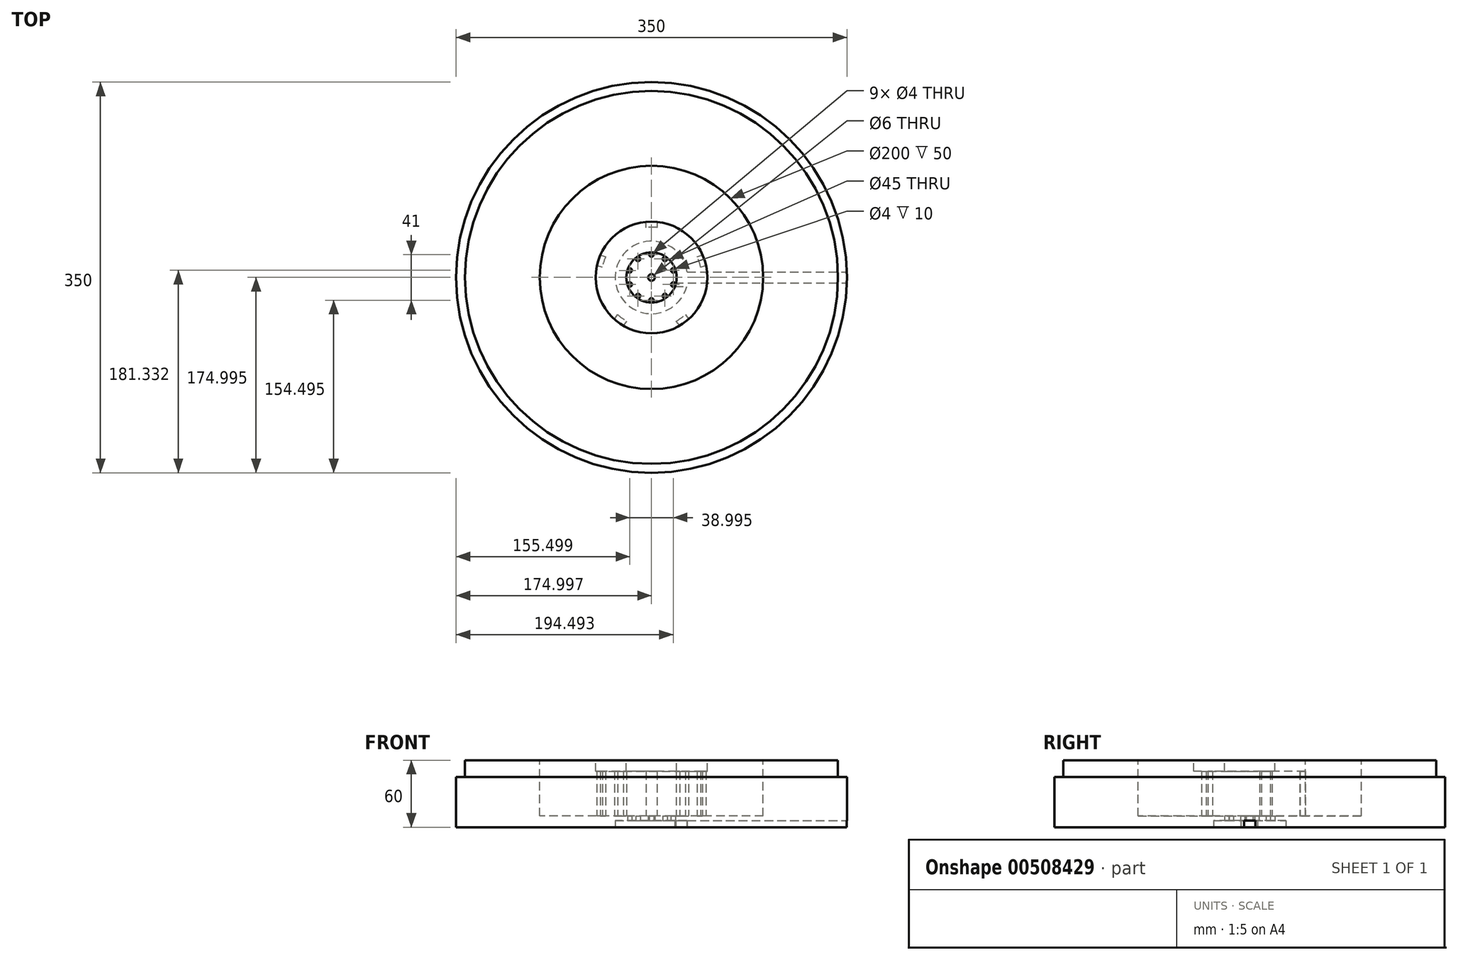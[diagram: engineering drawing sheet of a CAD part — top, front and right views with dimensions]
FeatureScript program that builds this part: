
annotation { "Feature Type Name" : "Feature", "Feature Type Description" : "" }
export const myFeature = defineFeature(function(context is Context, id is Id, definition is map)
    precondition{}
    {
        {
            var Q0;
            Q0=qCreatedBy(makeId("Top.planeOp"),FACE);
            var sketch = newSketch(context, id + "F0", { "sketchPlane" : qUnion([Q0])});
            skCircle(sketch, "E0", {"center": v(-44.55, -28.05) * mm, "radius": 167 * mm});
            skSolve(sketch);
        }
        {
            var Q0;
            Q0 = qSketchRegion(id + "F0", true);
            extrude(context, id + "F1", {"entities" : qUnion([Q0]), "depth" : 50 * mm});
        }
        {
            var Q0;
            Q0=makeQuery(id+"F1.opExtrude","CAP_FACE",FACE,{"disambiguationData":[OSD([sQuery(id+"F0.wireOp",EDGE,"E0")])],"isStart":false});
            var sketch = newSketch(context, id + "F2", { "sketchPlane" : qUnion([Q0])});
            skCircle(sketch, "E1", {"center": v(-44.55, -28.05) * mm, "radius": 168 * mm});
            skCircle(sketch, "E2", {"center": v(-44.55, -28.05) * mm, "radius": 22.5 * mm});
            skCircle(sketch, "E3", {"center": v(-44.55, -28.05) * mm, "radius": 100 * mm});
            skCircle(sketch, "E4", {"center": v(-44.55, -28.05) * mm, "radius": 50 * mm});
            skSolve(sketch);
        }
        {
            var Q0;
            Q0=makeQuery(id+"F2.imprint","IMPRINT",FACE,{"disambiguationData":[TD([[makeQuery(id+"F2.imprint","IMPRINT",EDGE,{"derivedFrom":sQuery(id+"F2.wireOp",EDGE,"E3")}),1.0]])]});
            var Q1;
            Q1=makeQuery(id+"F2.imprint","IMPRINT",FACE,{"disambiguationData":[TD([[makeQuery(id+"F2.imprint","IMPRINT",EDGE,{"derivedFrom":sQuery(id+"F2.wireOp",EDGE,"E2")}),1.0]])]});
            extrude(context, id + "F3", {"entities" : qUnion([Q0, Q1]), "operationType" : NewBodyOperationType.REMOVE, "oppositeDirection" : true, "depth" : 50 * mm});
        }
        {
            var Q0;
            Q0=makeQuery(id+"F3.boolean.opBoolean","SPLIT",FACE,{"disambiguationData":[TD([makeQuery(id+"F3.opExtrude","SWEPT_FACE",FACE,{"disambiguationData":[OSD([sQuery(id+"F2.wireOp",EDGE,"E2")])]})])],"derivedFrom":makeQuery(id+"F1.opExtrude","CAP_FACE",FACE,{"disambiguationData":[OSD([sQuery(id+"F0.wireOp",EDGE,"E0")])],"isStart":false})});
            var sketch = newSketch(context, id + "F4", { "sketchPlane" : qUnion([Q0])});
            skCircle(sketch, "E5", {"center": v(-44.55, -28.05) * mm, "radius": 100 * mm});
            skCircle(sketch, "E6", {"center": v(-44.55, -28.05) * mm, "radius": 50 * mm});
            skCircle(sketch, "E7", {"center": v(-44.55, -28.05) * mm, "radius": 10 * mm});
            skLineSegment(sketch, "E8", {"start": v(-44.55, 21.95) * mm, "end": v(-39.55, 21.95) * mm});
            skLineSegment(sketch, "E9", {"start": v(-39.55, 21.95) * mm, "end": v(-49.55, 21.95) * mm});
            skLineSegment(sketch, "E10", {"start": v(-49.55, 21.95) * mm, "end": v(-49.55, 71.82) * mm});
            skLineSegment(sketch, "E11", {"start": v(-49.55, 71.82) * mm, "end": v(-49.55, -19.4) * mm});
            skLineSegment(sketch, "E12", {"start": v(-49.55, -19.4) * mm, "end": v(-23.79, -19.4) * mm});
            skLineSegment(sketch, "E13", {"start": v(-23.79, -19.4) * mm, "end": v(-39.55, 21.95) * mm});
            skLineSegment(sketch, "E14", {"start": v(-39.55, 71.82) * mm, "end": v(-39.55, 21.95) * mm});
            skLineSegment(sketch, "E15.1.0", {"start": v(52.2, -2.8) * mm, "end": v(4.64, -17.79) * mm});
            skLineSegment(sketch, "E15.1.1", {"start": v(49.2, 6.75) * mm, "end": v(-37.8, -20.68) * mm});
            skLineSegment(sketch, "E15.1.2", {"start": v(-30.05, -45.26) * mm, "end": v(4.64, -17.79) * mm});
            skLineSegment(sketch, "E15.2.0", {"start": v(8.64, -112.74) * mm, "end": v(-19.97, -71.88) * mm});
            skLineSegment(sketch, "E15.2.1", {"start": v(16.83, -107) * mm, "end": v(-35.5, -32.28) * mm});
            skLineSegment(sketch, "E15.2.2", {"start": v(-56.6, -47.06) * mm, "end": v(-19.97, -71.88) * mm});
            skLineSegment(sketch, "E15.3.0", {"start": v(-109.32, -104.25) * mm, "end": v(-78.96, -64.68) * mm});
            skLineSegment(sketch, "E15.3.1", {"start": v(-101.39, -110.33) * mm, "end": v(-45.86, -37.97) * mm});
            skLineSegment(sketch, "E15.3.2", {"start": v(-66.3, -22.28) * mm, "end": v(-78.96, -64.68) * mm});
            skLineSegment(sketch, "E15.4.0", {"start": v(-136.7, 10.8) * mm, "end": v(-89.83, -6.26) * mm});
            skLineSegment(sketch, "E15.4.1", {"start": v(-140.12, 1.4) * mm, "end": v(-54.4, -29.8) * mm});
            skLineSegment(sketch, "E15.4.2", {"start": v(-45.59, -5.58) * mm, "end": v(-89.83, -6.26) * mm});
            skLineSegment(sketch, "E15.anchor1", {"start": v(-44.55, -28.05) * mm, "end": v(-39.55, 21.95) * mm, "construction": true});
            skLineSegment(sketch, "E15.anchor2", {"start": v(-44.55, -28.05) * mm, "end": v(-89.83, -6.26) * mm, "construction": true});
            skSolve(sketch);
        }
        {
            var Q0;
            {var subQ5=sQuery(id+"F4.wireOp",EDGE,"E15.1.0");Q0=makeQuery(id+"F4.imprint","IMPRINT",FACE,{"disambiguationData":[TD([[makeQuery(id+"F4.imprint","IMPRINT",EDGE,{"derivedFrom":subQ5}),-1.0]])]});}
            var Q1;
            {var subQ5=sQuery(id+"F4.wireOp",EDGE,"E15.4.0");Q1=makeQuery(id+"F4.imprint","IMPRINT",FACE,{"disambiguationData":[TD([[makeQuery(id+"F4.imprint","IMPRINT",EDGE,{"derivedFrom":subQ5}),-1.0]])]});}
            var Q2;
            {var subQ0=sQuery(id+"F4.wireOp",EDGE,"E15.3.0");Q2=makeQuery(id+"F4.imprint","IMPRINT",FACE,{"disambiguationData":[TD([[makeQuery(id+"F4.imprint","IMPRINT",EDGE,{"derivedFrom":subQ0}),-1.0]])]});}
            var Q3;
            {var subQ5=sQuery(id+"F4.wireOp",EDGE,"E15.2.0");Q3=makeQuery(id+"F4.imprint","IMPRINT",FACE,{"disambiguationData":[TD([[makeQuery(id+"F4.imprint","IMPRINT",EDGE,{"derivedFrom":subQ5}),-1.0]])]});}
            var Q4;
            {var subQ5=sQuery(id+"F4.wireOp",EDGE,"E14");Q4=makeQuery(id+"F4.imprint","IMPRINT",FACE,{"disambiguationData":[TD([[makeQuery(id+"F4.imprint","IMPRINT",EDGE,{"derivedFrom":subQ5}),-1.0]])]});}
            var Q5;
            {var subQ0=sQuery(id+"F4.wireOp",EDGE,"E13");var subQ1=sQuery(id+"F4.wireOp",EDGE,"E6");var subQ2=makeQuery(id+"F4.imprint","INTERSECT",VERTEX,{"derivedFrom":[subQ1,subQ0]});Q5=makeQuery(id+"F4.imprint","IMPRINT",FACE,{"disambiguationData":[TD([[makeQuery(id+"F4.imprint","IMPRINT",EDGE,{"disambiguationData":[TD([[subQ2,-1.0]])],"derivedFrom":subQ1}),-1.0]])]});}
            var Q6;
            {var subQ0=sQuery(id+"F4.wireOp",EDGE,"E9");var subQ1=sQuery(id+"F4.wireOp",EDGE,"E6");var subQ2=makeQuery(id+"F4.imprint","INTERSECT",VERTEX,{"derivedFrom":[subQ1,subQ0]});Q6=makeQuery(id+"F4.imprint","IMPRINT",FACE,{"disambiguationData":[TD([[makeQuery(id+"F4.imprint","IMPRINT",EDGE,{"disambiguationData":[TD([[subQ2,-1.0]])],"derivedFrom":subQ1}),-1.0]])]});}
            extrude(context, id + "F5", {"entities" : qUnion([Q0, Q1, Q2, Q3, Q4, Q5, Q6]), "operationType" : NewBodyOperationType.ADD, "oppositeDirection" : true, "depth" : 10 * mm, "hasDraft" : true, "draftAngle" : 3 * degree});
        }
        {
            var Q0;
            Q0=makeQuery(id+"F0.imprint","IMPRINT",FACE,{"disambiguationData":[TD([[makeQuery(id+"F0.imprint","IMPRINT",EDGE,{"derivedFrom":sQuery(id+"F0.wireOp",EDGE,"E0")}),1.0]])]});
            var sketch = newSketch(context, id + "F6", { "sketchPlane" : qUnion([Q0])});
            skCircle(sketch, "E16", {"center": v(-44.55, -28.05) * mm, "radius": 50 * mm});
            skCircle(sketch, "E17", {"center": v(-44.55, -28.05) * mm, "radius": 10 * mm});
            skLineSegment(sketch, "E18", {"start": v(-44.55, -28.05) * mm, "end": v(-44.55, 21.95) * mm});
            skLineSegment(sketch, "E19", {"start": v(-44.55, 21.95) * mm, "end": v(-49.55, 21.95) * mm});
            skLineSegment(sketch, "E20", {"start": v(-49.55, 21.95) * mm, "end": v(-39.55, 21.95) * mm});
            skLineSegment(sketch, "E21", {"start": v(-39.55, 21.95) * mm, "end": v(-39.55, -28.05) * mm});
            skLineSegment(sketch, "E22", {"start": v(-39.55, -28.05) * mm, "end": v(-49.55, -28.05) * mm});
            skLineSegment(sketch, "E23", {"start": v(-49.55, -28.05) * mm, "end": v(-49.55, 21.95) * mm});
            skCircle(sketch, "E24", {"center": v(-44.55, -28.05) * mm, "radius": 45 * mm});
            skLineSegment(sketch, "E25.1.0", {"start": v(-46.1, -32.81) * mm, "end": v(-93.65, -17.36) * mm});
            skLineSegment(sketch, "E25.1.1", {"start": v(-93.65, -17.36) * mm, "end": v(-90.56, -7.85) * mm});
            skLineSegment(sketch, "E25.1.3", {"start": v(-90.56, -7.85) * mm, "end": v(-43, -23.3) * mm});
            skLineSegment(sketch, "E25.2.0", {"start": v(-40.5, -31) * mm, "end": v(-69.9, -71.44) * mm});
            skLineSegment(sketch, "E25.2.1", {"start": v(-69.9, -71.44) * mm, "end": v(-77.99, -65.57) * mm});
            skLineSegment(sketch, "E25.2.3", {"start": v(-77.99, -65.57) * mm, "end": v(-48.6, -25.12) * mm});
            skLineSegment(sketch, "E25.3.0", {"start": v(-40.5, -25.12) * mm, "end": v(-11.12, -65.57) * mm});
            skLineSegment(sketch, "E25.3.1", {"start": v(-11.12, -65.57) * mm, "end": v(-19.2, -71.44) * mm});
            skLineSegment(sketch, "E25.3.3", {"start": v(-19.2, -71.44) * mm, "end": v(-48.6, -31) * mm});
            skLineSegment(sketch, "E25.4.0", {"start": v(-46.1, -23.3) * mm, "end": v(1.45, -7.85) * mm});
            skLineSegment(sketch, "E25.4.1", {"start": v(1.45, -7.85) * mm, "end": v(4.54, -17.36) * mm});
            skLineSegment(sketch, "E25.4.3", {"start": v(4.54, -17.36) * mm, "end": v(-43, -32.81) * mm});
            skSolve(sketch);
        }
        {
            var Q0;
            Q0=makeQuery(id+"F6.imprint","IMPRINT",FACE,{"disambiguationData":[TD([[makeQuery(id+"F6.imprint","IMPRINT",EDGE,{"derivedFrom":makeQuery(id+"F0.imprint","IMPRINT",EDGE,{"derivedFrom":sQuery(id+"F0.wireOp",EDGE,"E0")})}),1.0]])]});
            var sketch = newSketch(context, id + "F7", { "sketchPlane" : qUnion([Q0])});
            skSolve(sketch);
        }
        {
            var Q0;
            {var subQ0=sQuery(id+"F6.wireOp",EDGE,"E25.1.0");var subQ1=sQuery(id+"F6.wireOp",EDGE,"E17");var subQ2=makeQuery(id+"F6.imprint","INTERSECT",VERTEX,{"derivedFrom":[subQ1,subQ0]});Q0=makeQuery(id+"F6.imprint","IMPRINT",FACE,{"disambiguationData":[TD([[makeQuery(id+"F6.imprint","IMPRINT",EDGE,{"disambiguationData":[TD([[subQ2,-1.0]])],"derivedFrom":subQ1}),-1.0]])]});}
            var Q1;
            {var subQ0=sQuery(id+"F6.wireOp",EDGE,"E21");var subQ1=sQuery(id+"F6.wireOp",EDGE,"E17");var subQ2=makeQuery(id+"F6.imprint","INTERSECT",VERTEX,{"derivedFrom":[subQ1,subQ0]});Q1=makeQuery(id+"F6.imprint","IMPRINT",FACE,{"disambiguationData":[TD([[makeQuery(id+"F6.imprint","IMPRINT",EDGE,{"disambiguationData":[TD([[subQ2,1.0]])],"derivedFrom":subQ1}),-1.0]])]});}
            var Q2;
            {var subQ0=sQuery(id+"F6.wireOp",EDGE,"E21");var subQ1=sQuery(id+"F6.wireOp",EDGE,"E17");var subQ2=makeQuery(id+"F6.imprint","INTERSECT",VERTEX,{"derivedFrom":[subQ1,subQ0]});Q2=makeQuery(id+"F6.imprint","IMPRINT",FACE,{"disambiguationData":[TD([[makeQuery(id+"F6.imprint","IMPRINT",EDGE,{"disambiguationData":[TD([[subQ2,-1.0]])],"derivedFrom":subQ1}),-1.0]])]});}
            var Q3;
            {var subQ0=sQuery(id+"F6.wireOp",EDGE,"E18");var subQ1=sQuery(id+"F6.wireOp",EDGE,"E17");var subQ2=makeQuery(id+"F6.imprint","INTERSECT",VERTEX,{"derivedFrom":[subQ1,subQ0]});Q3=makeQuery(id+"F6.imprint","IMPRINT",FACE,{"disambiguationData":[TD([[makeQuery(id+"F6.imprint","IMPRINT",EDGE,{"disambiguationData":[TD([[subQ2,-1.0]])],"derivedFrom":subQ1}),-1.0]])]});}
            var Q4;
            {var subQ0=sQuery(id+"F6.wireOp",EDGE,"E23");var subQ1=sQuery(id+"F6.wireOp",EDGE,"E17");var subQ2=makeQuery(id+"F6.imprint","INTERSECT",VERTEX,{"derivedFrom":[subQ1,subQ0]});Q4=makeQuery(id+"F6.imprint","IMPRINT",FACE,{"disambiguationData":[TD([[makeQuery(id+"F6.imprint","IMPRINT",EDGE,{"disambiguationData":[TD([[subQ2,-1.0]])],"derivedFrom":subQ1}),-1.0]])]});}
            var Q5;
            {var subQ0=sQuery(id+"F6.wireOp",EDGE,"E25.1.3");var subQ1=sQuery(id+"F6.wireOp",EDGE,"E17");var subQ2=makeQuery(id+"F6.imprint","INTERSECT",VERTEX,{"derivedFrom":[subQ1,subQ0]});Q5=makeQuery(id+"F6.imprint","IMPRINT",FACE,{"disambiguationData":[TD([[makeQuery(id+"F6.imprint","IMPRINT",EDGE,{"disambiguationData":[TD([[subQ2,-1.0]])],"derivedFrom":subQ1}),-1.0]])]});}
            var Q6;
            {var subQ0=sQuery(id+"F6.wireOp",EDGE,"E25.2.3");var subQ1=sQuery(id+"F6.wireOp",EDGE,"E17");var subQ2=makeQuery(id+"F6.imprint","INTERSECT",VERTEX,{"derivedFrom":[subQ1,subQ0]});Q6=makeQuery(id+"F6.imprint","IMPRINT",FACE,{"disambiguationData":[TD([[makeQuery(id+"F6.imprint","IMPRINT",EDGE,{"disambiguationData":[TD([[subQ2,-1.0]])],"derivedFrom":subQ1}),-1.0]])]});}
            var Q7;
            {var subQ0=sQuery(id+"F6.wireOp",EDGE,"E25.2.0");var subQ1=sQuery(id+"F6.wireOp",EDGE,"E16");var subQ2=makeQuery(id+"F6.imprint","INTERSECT",VERTEX,{"derivedFrom":[subQ1,subQ0]});Q7=makeQuery(id+"F6.imprint","IMPRINT",FACE,{"disambiguationData":[TD([[makeQuery(id+"F6.imprint","IMPRINT",EDGE,{"disambiguationData":[TD([[subQ2,-1.0]])],"derivedFrom":subQ1}),1.0]])]});}
            var Q8;
            {var subQ0=sQuery(id+"F6.wireOp",EDGE,"E25.2.0");var subQ1=sQuery(id+"F6.wireOp",EDGE,"E17");var subQ2=makeQuery(id+"F6.imprint","INTERSECT",VERTEX,{"derivedFrom":[subQ1,subQ0]});Q8=makeQuery(id+"F6.imprint","IMPRINT",FACE,{"disambiguationData":[TD([[makeQuery(id+"F6.imprint","IMPRINT",EDGE,{"disambiguationData":[TD([[subQ2,-1.0]])],"derivedFrom":subQ1}),-1.0]])]});}
            var Q9;
            {var subQ0=sQuery(id+"F6.wireOp",EDGE,"E25.3.3");var subQ1=sQuery(id+"F6.wireOp",EDGE,"E17");var subQ2=makeQuery(id+"F6.imprint","INTERSECT",VERTEX,{"derivedFrom":[subQ1,subQ0]});Q9=makeQuery(id+"F6.imprint","IMPRINT",FACE,{"disambiguationData":[TD([[makeQuery(id+"F6.imprint","IMPRINT",EDGE,{"disambiguationData":[TD([[subQ2,-1.0]])],"derivedFrom":subQ1}),-1.0]])]});}
            var Q10;
            {var subQ0=sQuery(id+"F6.wireOp",EDGE,"E25.3.0");var subQ1=sQuery(id+"F6.wireOp",EDGE,"E17");var subQ2=makeQuery(id+"F6.imprint","INTERSECT",VERTEX,{"derivedFrom":[subQ1,subQ0]});Q10=makeQuery(id+"F6.imprint","IMPRINT",FACE,{"disambiguationData":[TD([[makeQuery(id+"F6.imprint","IMPRINT",EDGE,{"disambiguationData":[TD([[subQ2,-1.0]])],"derivedFrom":subQ1}),-1.0]])]});}
            var Q11;
            {var subQ0=sQuery(id+"F6.wireOp",EDGE,"E25.4.0");var subQ1=sQuery(id+"F6.wireOp",EDGE,"E17");var subQ2=makeQuery(id+"F6.imprint","INTERSECT",VERTEX,{"derivedFrom":[subQ1,subQ0]});Q11=makeQuery(id+"F6.imprint","IMPRINT",FACE,{"disambiguationData":[TD([[makeQuery(id+"F6.imprint","IMPRINT",EDGE,{"disambiguationData":[TD([[subQ2,1.0]])],"derivedFrom":subQ1}),-1.0]])]});}
            var Q12;
            {var subQ0=sQuery(id+"F6.wireOp",EDGE,"E25.4.3");var subQ1=sQuery(id+"F6.wireOp",EDGE,"E16");var subQ2=makeQuery(id+"F6.imprint","INTERSECT",VERTEX,{"derivedFrom":[subQ1,subQ0]});Q12=makeQuery(id+"F6.imprint","IMPRINT",FACE,{"disambiguationData":[TD([[makeQuery(id+"F6.imprint","IMPRINT",EDGE,{"disambiguationData":[TD([[subQ2,1.0]])],"derivedFrom":subQ1}),1.0]])]});}
            var Q13;
            {var subQ0=sQuery(id+"F6.wireOp",EDGE,"E25.4.0");var subQ1=sQuery(id+"F6.wireOp",EDGE,"E16");var subQ2=makeQuery(id+"F6.imprint","INTERSECT",VERTEX,{"derivedFrom":[subQ1,subQ0]});Q13=makeQuery(id+"F6.imprint","IMPRINT",FACE,{"disambiguationData":[TD([[makeQuery(id+"F6.imprint","IMPRINT",EDGE,{"disambiguationData":[TD([[subQ2,-1.0]])],"derivedFrom":subQ1}),1.0]])]});}
            var Q14;
            {var subQ0=sQuery(id+"F6.wireOp",EDGE,"E23");var subQ1=sQuery(id+"F6.wireOp",EDGE,"E16");var subQ2=makeQuery(id+"F6.imprint","INTERSECT",VERTEX,{"derivedFrom":[subQ1,subQ0]});Q14=makeQuery(id+"F6.imprint","IMPRINT",FACE,{"disambiguationData":[TD([[makeQuery(id+"F6.imprint","IMPRINT",EDGE,{"disambiguationData":[TD([[subQ2,-1.0]])],"derivedFrom":subQ1}),1.0]])]});}
            var Q15;
            {var subQ0=sQuery(id+"F6.wireOp",EDGE,"E25.1.0");var subQ1=sQuery(id+"F6.wireOp",EDGE,"E16");var subQ2=makeQuery(id+"F6.imprint","INTERSECT",VERTEX,{"derivedFrom":[subQ1,subQ0]});Q15=makeQuery(id+"F6.imprint","IMPRINT",FACE,{"disambiguationData":[TD([[makeQuery(id+"F6.imprint","IMPRINT",EDGE,{"disambiguationData":[TD([[subQ2,-1.0]])],"derivedFrom":subQ1}),1.0]])]});}
            extrude(context, id + "F8", {"entities" : qUnion([Q0, Q1, Q2, Q3, Q4, Q5, Q6, Q7, Q8, Q9, Q10, Q11, Q12, Q13, Q14, Q15]), "operationType" : NewBodyOperationType.REMOVE, "depth" : 40 * mm});
        }
        {
            var Q0;
            Q0=makeQuery(id+"F7.imprint","IMPRINT",FACE,{"disambiguationData":[TD([[makeQuery(id+"F7.imprint","IMPRINT",EDGE,{"derivedFrom":makeQuery(id+"F6.imprint","IMPRINT",EDGE,{"derivedFrom":makeQuery(id+"F0.imprint","IMPRINT",EDGE,{"derivedFrom":sQuery(id+"F0.wireOp",EDGE,"E0")})})}),1.0]])]});
            var sketch = newSketch(context, id + "F9", { "sketchPlane" : qUnion([Q0])});
            skCircle(sketch, "E26", {"center": v(-44.55, -28.05) * mm, "radius": 100 * mm});
            skCircle(sketch, "E27", {"center": v(-44.55, -28.05) * mm, "radius": 167 * mm});
            skCircle(sketch, "E28", {"center": v(-44.55, -28.05) * mm, "radius": 10 * mm});
            skCircle(sketch, "E29", {"center": v(-44.55, -28.05) * mm, "radius": 50 * mm});
            skSolve(sketch);
        }
        {
            var Q0;
            Q0 = qSketchRegion(id + "F9", true);
            var Q1;
            Q1=makeQuery(id+"F9.imprint","IMPRINT",FACE,{"disambiguationData":[TD([[makeQuery(id+"F9.imprint","IMPRINT",EDGE,{"derivedFrom":sQuery(id+"F9.wireOp",EDGE,"E26")}),1.0]])]});
            var Q2;
            {var subQ1=sQuery(id+"F6.wireOp",EDGE,"E25.4.0");var subQ3=sQuery(id+"F6.wireOp",EDGE,"E16");var subQ4=makeQuery(id+"F6.imprint","INTERSECT",VERTEX,{"derivedFrom":[subQ3,subQ1]});Q2=makeQuery(id+"F7.imprint","IMPRINT",FACE,{"disambiguationData":[TD([[makeQuery(id+"F7.imprint","IMPRINT",EDGE,{"derivedFrom":makeQuery(id+"F6.imprint","IMPRINT",EDGE,{"disambiguationData":[TD([[subQ4,-1.0]])],"derivedFrom":subQ3})}),1.0]])]});}
            extrude(context, id + "F10", {"entities" : qUnion([Q0, Q1, Q2]), "operationType" : NewBodyOperationType.ADD, "oppositeDirection" : true, "depth" : 10 * mm});
        }
        {
            var Q0;
            {var subQ0=sQuery(id+"F4.wireOp",EDGE,"E6");var subQ1=sQuery(id+"F4.wireOp",EDGE,"E5");var subQ2=sQuery(id+"F0.wireOp",EDGE,"E0");var subQ3=makeQuery(id+"F1.opExtrude","CAP_FACE",FACE,{"disambiguationData":[OSD([subQ2])],"isStart":false});Q0=makeQuery(id+"F5.boolean.opBoolean","MERGE",FACE,{"derivedFrom":[makeQuery(id+"F3.boolean.opBoolean","SPLIT",FACE,{"disambiguationData":[TD([makeQuery(id+"F1.opExtrude","SWEPT_FACE",FACE,{"disambiguationData":[OSD([subQ2])]})])],"derivedFrom":subQ3}),makeQuery(id+"F3.boolean.opBoolean","SPLIT",FACE,{"disambiguationData":[TD([makeQuery(id+"F3.opExtrude","SWEPT_FACE",FACE,{"disambiguationData":[OSD([sQuery(id+"F2.wireOp",EDGE,"E2")])]})])],"derivedFrom":subQ3}),makeQuery(id+"F5.opExtrude","CAP_FACE",FACE,{"disambiguationData":[OSD([subQ1,subQ0,sQuery(id+"F4.wireOp",EDGE,"E15.1.0"),sQuery(id+"F4.wireOp",EDGE,"E15.1.1"),sQuery(id+"F4.wireOp",EDGE,"E15.1.2")])],"isStart":true}),makeQuery(id+"F5.opExtrude","CAP_FACE",FACE,{"disambiguationData":[OSD([subQ1,subQ0,sQuery(id+"F4.wireOp",EDGE,"E11"),sQuery(id+"F4.wireOp",EDGE,"E13"),sQuery(id+"F4.wireOp",EDGE,"E14")])],"isStart":true}),makeQuery(id+"F5.opExtrude","CAP_FACE",FACE,{"disambiguationData":[OSD([subQ1,subQ0,sQuery(id+"F4.wireOp",EDGE,"E15.4.0"),sQuery(id+"F4.wireOp",EDGE,"E15.4.1"),sQuery(id+"F4.wireOp",EDGE,"E15.4.2")])],"isStart":true}),makeQuery(id+"F5.opExtrude","CAP_FACE",FACE,{"disambiguationData":[OSD([subQ1,subQ0,sQuery(id+"F4.wireOp",EDGE,"E15.3.0"),sQuery(id+"F4.wireOp",EDGE,"E15.3.1"),sQuery(id+"F4.wireOp",EDGE,"E15.3.2")])],"isStart":true}),makeQuery(id+"F5.opExtrude","CAP_FACE",FACE,{"disambiguationData":[OSD([subQ1,subQ0,sQuery(id+"F4.wireOp",EDGE,"E15.2.0"),sQuery(id+"F4.wireOp",EDGE,"E15.2.1"),sQuery(id+"F4.wireOp",EDGE,"E15.2.2")])],"isStart":true})]});}
            var sketch = newSketch(context, id + "F11", { "sketchPlane" : qUnion([Q0])});
            skCircle(sketch, "E30", {"center": v(-44.55, -28.05) * mm, "radius": 100 * mm});
            skCircle(sketch, "E31", {"center": v(-44.55, -28.05) * mm, "radius": 50 * mm});
            skSolve(sketch);
        }
        {
            var Q0;
            Q0 = qSketchRegion(id + "F11", true);
            extrude(context, id + "F12", {"entities" : qUnion([Q0]), "operationType" : NewBodyOperationType.REMOVE, "oppositeDirection" : true, "depth" : 33 * mm});
        }
        {
            var Q0;
            {var subQ0=sQuery(id+"F6.wireOp",EDGE,"E25.4.3");var subQ1=sQuery(id+"F6.wireOp",EDGE,"E25.4.1");var subQ2=sQuery(id+"F6.wireOp",EDGE,"E25.4.0");var subQ3=sQuery(id+"F6.wireOp",EDGE,"E25.3.3");var subQ4=sQuery(id+"F6.wireOp",EDGE,"E25.3.1");var subQ5=sQuery(id+"F6.wireOp",EDGE,"E25.3.0");var subQ6=sQuery(id+"F6.wireOp",EDGE,"E25.2.3");var subQ7=sQuery(id+"F6.wireOp",EDGE,"E25.2.1");var subQ8=sQuery(id+"F6.wireOp",EDGE,"E25.2.0");var subQ9=sQuery(id+"F6.wireOp",EDGE,"E25.1.3");var subQ10=sQuery(id+"F6.wireOp",EDGE,"E25.1.1");var subQ11=sQuery(id+"F6.wireOp",EDGE,"E25.1.0");var subQ12=sQuery(id+"F6.wireOp",EDGE,"E23");var subQ13=sQuery(id+"F6.wireOp",EDGE,"E21");var subQ14=sQuery(id+"F6.wireOp",EDGE,"E20");Q0=makeQuery(id+"F10.boolean.opBoolean","MERGE",FACE,{"derivedFrom":[makeQuery(id+"F10.opExtrude","CAP_FACE",FACE,{"disambiguationData":[OSD([sQuery(id+"F6.wireOp",EDGE,"E16"),subQ14,subQ13,subQ12,subQ11,subQ10,subQ9,subQ8,subQ7,subQ6,subQ5,subQ4,subQ3,subQ2,subQ1,subQ0])],"isStart":false}),makeQuery(id+"F10.opExtrude","CAP_FACE",FACE,{"disambiguationData":[OSD([subQ14,subQ13,subQ12,subQ11,subQ10,subQ9,subQ8,subQ7,subQ6,subQ5,subQ4,subQ3,subQ2,subQ1,subQ0,sQuery(id+"F9.wireOp",EDGE,"E27"),sQuery(id+"F9.wireOp",EDGE,"E29")])],"isStart":false})]});}
            var sketch = newSketch(context, id + "F13", { "sketchPlane" : qUnion([Q0])});
            skCircle(sketch, "E32", {"center": v(-44.55, 28.05) * mm, "radius": 167 * mm});
            skCircle(sketch, "E33", {"center": v(-44.55, 28.05) * mm, "radius": 175 * mm});
            skSolve(sketch);
        }
        {
            var Q0;
            Q0 = qSketchRegion(id + "F13", true);
            extrude(context, id + "F14", {"entities" : qUnion([Q0]), "operationType" : NewBodyOperationType.ADD, "oppositeDirection" : true, "depth" : 45 * mm});
        }
        {
            var Q0;
            {var subQ0=sQuery(id+"F6.wireOp",EDGE,"E25.4.3");var subQ1=sQuery(id+"F6.wireOp",EDGE,"E25.4.1");var subQ2=sQuery(id+"F6.wireOp",EDGE,"E25.4.0");var subQ3=sQuery(id+"F6.wireOp",EDGE,"E25.3.3");var subQ4=sQuery(id+"F6.wireOp",EDGE,"E25.3.1");var subQ5=sQuery(id+"F6.wireOp",EDGE,"E25.3.0");var subQ6=sQuery(id+"F6.wireOp",EDGE,"E25.2.3");var subQ7=sQuery(id+"F6.wireOp",EDGE,"E25.2.1");var subQ8=sQuery(id+"F6.wireOp",EDGE,"E25.2.0");var subQ9=sQuery(id+"F6.wireOp",EDGE,"E25.1.3");var subQ10=sQuery(id+"F6.wireOp",EDGE,"E25.1.1");var subQ11=sQuery(id+"F6.wireOp",EDGE,"E25.1.0");var subQ12=sQuery(id+"F6.wireOp",EDGE,"E23");var subQ13=sQuery(id+"F6.wireOp",EDGE,"E21");var subQ14=sQuery(id+"F6.wireOp",EDGE,"E20");Q0=makeQuery(id+"F14.boolean.opBoolean","MERGE",FACE,{"derivedFrom":[makeQuery(id+"F10.boolean.opBoolean","MERGE",FACE,{"derivedFrom":[makeQuery(id+"F10.opExtrude","CAP_FACE",FACE,{"disambiguationData":[OSD([sQuery(id+"F6.wireOp",EDGE,"E16"),subQ14,subQ13,subQ12,subQ11,subQ10,subQ9,subQ8,subQ7,subQ6,subQ5,subQ4,subQ3,subQ2,subQ1,subQ0])],"isStart":false}),makeQuery(id+"F10.opExtrude","CAP_FACE",FACE,{"disambiguationData":[OSD([subQ14,subQ13,subQ12,subQ11,subQ10,subQ9,subQ8,subQ7,subQ6,subQ5,subQ4,subQ3,subQ2,subQ1,subQ0,sQuery(id+"F9.wireOp",EDGE,"E27"),sQuery(id+"F9.wireOp",EDGE,"E29")])],"isStart":false})]}),makeQuery(id+"F14.opExtrude","CAP_FACE",FACE,{"disambiguationData":[OSD([sQuery(id+"F13.wireOp",EDGE,"E32"),sQuery(id+"F13.wireOp",EDGE,"E33")])],"isStart":true})]});}
            var sketch = newSketch(context, id + "F15", { "sketchPlane" : qUnion([Q0])});
            skCircle(sketch, "E34", {"center": v(-44.55, 28.05) * mm, "radius": 175 * mm});
            skCircle(sketch, "E35", {"center": v(-44.55, 28.05) * mm, "radius": 3 * mm});
            skSolve(sketch);
        }
        {
            var Q0;
            Q0=makeQuery(id+"F15.imprint","IMPRINT",FACE,{"disambiguationData":[TD([[makeQuery(id+"F15.imprint","IMPRINT",EDGE,{"derivedFrom":sQuery(id+"F15.wireOp",EDGE,"E35")}),1.0]])]});
            extrude(context, id + "F16", {"entities" : qUnion([Q0]), "operationType" : NewBodyOperationType.REMOVE, "oppositeDirection" : true, "depth" : 151 * mm});
        }
        {
            var Q0;
            {var subQ0=sQuery(id+"F6.wireOp",EDGE,"E25.4.3");var subQ1=sQuery(id+"F6.wireOp",EDGE,"E25.4.1");var subQ2=sQuery(id+"F6.wireOp",EDGE,"E25.4.0");var subQ3=sQuery(id+"F6.wireOp",EDGE,"E25.3.3");var subQ4=sQuery(id+"F6.wireOp",EDGE,"E25.3.1");var subQ5=sQuery(id+"F6.wireOp",EDGE,"E25.3.0");var subQ6=sQuery(id+"F6.wireOp",EDGE,"E25.2.3");var subQ7=sQuery(id+"F6.wireOp",EDGE,"E25.2.1");var subQ8=sQuery(id+"F6.wireOp",EDGE,"E25.2.0");var subQ9=sQuery(id+"F6.wireOp",EDGE,"E25.1.3");var subQ10=sQuery(id+"F6.wireOp",EDGE,"E25.1.1");var subQ11=sQuery(id+"F6.wireOp",EDGE,"E25.1.0");var subQ12=sQuery(id+"F6.wireOp",EDGE,"E23");var subQ13=sQuery(id+"F6.wireOp",EDGE,"E21");var subQ14=sQuery(id+"F6.wireOp",EDGE,"E20");Q0=makeQuery(id+"F14.boolean.opBoolean","MERGE",FACE,{"derivedFrom":[makeQuery(id+"F10.boolean.opBoolean","MERGE",FACE,{"derivedFrom":[makeQuery(id+"F10.opExtrude","CAP_FACE",FACE,{"disambiguationData":[OSD([sQuery(id+"F6.wireOp",EDGE,"E16"),subQ14,subQ13,subQ12,subQ11,subQ10,subQ9,subQ8,subQ7,subQ6,subQ5,subQ4,subQ3,subQ2,subQ1,subQ0])],"isStart":false}),makeQuery(id+"F10.opExtrude","CAP_FACE",FACE,{"disambiguationData":[OSD([subQ14,subQ13,subQ12,subQ11,subQ10,subQ9,subQ8,subQ7,subQ6,subQ5,subQ4,subQ3,subQ2,subQ1,subQ0,sQuery(id+"F9.wireOp",EDGE,"E27"),sQuery(id+"F9.wireOp",EDGE,"E29")])],"isStart":false})]}),makeQuery(id+"F14.opExtrude","CAP_FACE",FACE,{"disambiguationData":[OSD([sQuery(id+"F13.wireOp",EDGE,"E32"),sQuery(id+"F13.wireOp",EDGE,"E33")])],"isStart":true})]});}
            var sketch = newSketch(context, id + "F17", { "sketchPlane" : qUnion([Q0])});
            skLineSegment(sketch, "E36.bottom", {"start": v(-44.55, 28.05) * mm, "end": v(153.3, 28.05) * mm});
            skLineSegment(sketch, "E36.top", {"start": v(-44.55, 33.05) * mm, "end": v(153.3, 33.05) * mm});
            skLineSegment(sketch, "E36.left", {"start": v(-44.55, 28.05) * mm, "end": v(-44.55, 33.05) * mm});
            skLineSegment(sketch, "E36.right", {"start": v(153.3, 28.05) * mm, "end": v(153.3, 33.05) * mm});
            skLineSegment(sketch, "E37.bottom", {"start": v(-44.55, 28.05) * mm, "end": v(156.7, 28.05) * mm});
            skLineSegment(sketch, "E37.top", {"start": v(-44.55, 23.05) * mm, "end": v(156.7, 23.05) * mm});
            skLineSegment(sketch, "E37.left", {"start": v(-44.55, 28.05) * mm, "end": v(-44.55, 23.05) * mm});
            skLineSegment(sketch, "E37.right", {"start": v(156.7, 28.05) * mm, "end": v(156.7, 23.05) * mm});
            skSolve(sketch);
        }
        {
            var Q0;
            Q0 = qSketchRegion(id + "F17", true);
            extrude(context, id + "F18", {"entities" : qUnion([Q0]), "operationType" : NewBodyOperationType.REMOVE, "oppositeDirection" : true, "depth" : 6 * mm});
        }
        {
            var Q0;
            {var subQ0=sQuery(id+"F6.wireOp",EDGE,"E25.4.3");var subQ1=sQuery(id+"F6.wireOp",EDGE,"E25.4.1");var subQ2=sQuery(id+"F6.wireOp",EDGE,"E25.4.0");var subQ3=sQuery(id+"F6.wireOp",EDGE,"E25.3.3");var subQ4=sQuery(id+"F6.wireOp",EDGE,"E25.3.1");var subQ5=sQuery(id+"F6.wireOp",EDGE,"E25.3.0");var subQ6=sQuery(id+"F6.wireOp",EDGE,"E25.2.3");var subQ7=sQuery(id+"F6.wireOp",EDGE,"E25.2.1");var subQ8=sQuery(id+"F6.wireOp",EDGE,"E25.2.0");var subQ9=sQuery(id+"F6.wireOp",EDGE,"E25.1.3");var subQ10=sQuery(id+"F6.wireOp",EDGE,"E25.1.1");var subQ11=sQuery(id+"F6.wireOp",EDGE,"E25.1.0");var subQ12=sQuery(id+"F6.wireOp",EDGE,"E23");var subQ13=sQuery(id+"F6.wireOp",EDGE,"E21");var subQ14=sQuery(id+"F6.wireOp",EDGE,"E20");Q0=makeQuery(id+"F14.boolean.opBoolean","MERGE",FACE,{"derivedFrom":[makeQuery(id+"F10.boolean.opBoolean","MERGE",FACE,{"derivedFrom":[makeQuery(id+"F10.opExtrude","CAP_FACE",FACE,{"disambiguationData":[OSD([sQuery(id+"F6.wireOp",EDGE,"E16"),subQ14,subQ13,subQ12,subQ11,subQ10,subQ9,subQ8,subQ7,subQ6,subQ5,subQ4,subQ3,subQ2,subQ1,subQ0])],"isStart":false}),makeQuery(id+"F10.opExtrude","CAP_FACE",FACE,{"disambiguationData":[OSD([subQ14,subQ13,subQ12,subQ11,subQ10,subQ9,subQ8,subQ7,subQ6,subQ5,subQ4,subQ3,subQ2,subQ1,subQ0,sQuery(id+"F9.wireOp",EDGE,"E27"),sQuery(id+"F9.wireOp",EDGE,"E29")])],"isStart":false})]}),makeQuery(id+"F14.opExtrude","CAP_FACE",FACE,{"disambiguationData":[OSD([sQuery(id+"F13.wireOp",EDGE,"E32"),sQuery(id+"F13.wireOp",EDGE,"E33")])],"isStart":true})]});}
            var sketch = newSketch(context, id + "F19", { "sketchPlane" : qUnion([Q0])});
            skCircle(sketch, "E38", {"center": v(-25.06, 34.39) * mm, "radius": 2 * mm});
            skCircle(sketch, "E39.1.0", {"center": v(-32.5, 44.64) * mm, "radius": 2 * mm});
            skCircle(sketch, "E39.2.0", {"center": v(-44.55, 48.55) * mm, "radius": 2 * mm});
            skCircle(sketch, "E39.3.0", {"center": v(-56.6, 44.64) * mm, "radius": 2 * mm});
            skCircle(sketch, "E39.4.0", {"center": v(-64.05, 34.4) * mm, "radius": 2 * mm});
            skCircle(sketch, "E39.5.0", {"center": v(-64.05, 21.72) * mm, "radius": 2 * mm});
            skCircle(sketch, "E39.6.0", {"center": v(-56.6, 11.47) * mm, "radius": 2 * mm});
            skCircle(sketch, "E39.7.0", {"center": v(-44.56, 7.55) * mm, "radius": 2 * mm});
            skCircle(sketch, "E39.8.0", {"center": v(-32.5, 11.47) * mm, "radius": 2 * mm});
            skCircle(sketch, "E39.9.0", {"center": v(-25.06, 21.72) * mm, "radius": 2 * mm});
            skPoint(sketch, "E39.center", {"position": v(-44.55, 28.05) * mm});
            skLineSegment(sketch, "E40", {"start": v(-24.53, 32.46) * mm, "end": v(-24.38, 33.05) * mm});
            skLineSegment(sketch, "E41", {"start": v(-24.38, 33.05) * mm, "end": v(-24.27, 23.05) * mm});
            skLineSegment(sketch, "E42", {"start": v(-24.27, 23.05) * mm, "end": v(-24.48, 23.63) * mm});
            skSolve(sketch);
        }
        {
            var Q0;
            Q0 = qSketchRegion(id + "F19", true);
            extrude(context, id + "F20", {"entities" : qUnion([Q0]), "operationType" : NewBodyOperationType.REMOVE, "oppositeDirection" : true, "depth" : 219 * mm});
        }
        {
            var Q0;
            {var subQ0=sQuery(id+"F6.wireOp",EDGE,"E25.4.3");var subQ1=sQuery(id+"F6.wireOp",EDGE,"E25.4.1");var subQ2=sQuery(id+"F6.wireOp",EDGE,"E25.4.0");var subQ3=sQuery(id+"F6.wireOp",EDGE,"E25.3.3");var subQ4=sQuery(id+"F6.wireOp",EDGE,"E25.3.1");var subQ5=sQuery(id+"F6.wireOp",EDGE,"E25.3.0");var subQ6=sQuery(id+"F6.wireOp",EDGE,"E25.2.3");var subQ7=sQuery(id+"F6.wireOp",EDGE,"E25.2.1");var subQ8=sQuery(id+"F6.wireOp",EDGE,"E25.2.0");var subQ9=sQuery(id+"F6.wireOp",EDGE,"E25.1.3");var subQ10=sQuery(id+"F6.wireOp",EDGE,"E25.1.1");var subQ11=sQuery(id+"F6.wireOp",EDGE,"E25.1.0");var subQ12=sQuery(id+"F6.wireOp",EDGE,"E23");var subQ13=sQuery(id+"F6.wireOp",EDGE,"E21");var subQ14=sQuery(id+"F6.wireOp",EDGE,"E20");Q0=makeQuery(id+"F14.boolean.opBoolean","MERGE",FACE,{"derivedFrom":[makeQuery(id+"F10.boolean.opBoolean","MERGE",FACE,{"derivedFrom":[makeQuery(id+"F10.opExtrude","CAP_FACE",FACE,{"disambiguationData":[OSD([sQuery(id+"F6.wireOp",EDGE,"E16"),subQ14,subQ13,subQ12,subQ11,subQ10,subQ9,subQ8,subQ7,subQ6,subQ5,subQ4,subQ3,subQ2,subQ1,subQ0])],"isStart":false}),makeQuery(id+"F10.opExtrude","CAP_FACE",FACE,{"disambiguationData":[OSD([subQ14,subQ13,subQ12,subQ11,subQ10,subQ9,subQ8,subQ7,subQ6,subQ5,subQ4,subQ3,subQ2,subQ1,subQ0,sQuery(id+"F9.wireOp",EDGE,"E27"),sQuery(id+"F9.wireOp",EDGE,"E29")])],"isStart":false})]}),makeQuery(id+"F14.opExtrude","CAP_FACE",FACE,{"disambiguationData":[OSD([sQuery(id+"F13.wireOp",EDGE,"E32"),sQuery(id+"F13.wireOp",EDGE,"E33")])],"isStart":true})]});}
            var sketch = newSketch(context, id + "F21", { "sketchPlane" : qUnion([Q0])});
            skCircle(sketch, "E43", {"center": v(-44.55, 28.05) * mm, "radius": 22.5 * mm});
            skCircle(sketch, "E44.0", {"center": v(-44.55, 28.05) * mm, "radius": 32.5 * mm});
            skArc(sketch, "E45.0", {"start": v(-44.55, 20.05) * mm, "mid": v(-52.55, 28.05) * mm, "end": v(-44.55, 36.05) * mm});
            skLineSegment(sketch, "E45.1", {"start": v(125.26, 20.05) * mm, "end": v(-44.55, 20.05) * mm});
            skArc(sketch, "E45.2", {"start": v(125.26, 36.05) * mm, "mid": v(-214.55, 28.05) * mm, "end": v(125.26, 20.05) * mm});
            skLineSegment(sketch, "E45.3", {"start": v(-44.55, 36.05) * mm, "end": v(125.26, 36.05) * mm});
            skSolve(sketch);
        }
        {
            var Q0;
            {var subQ1=sQuery(id+"F21.wireOp",EDGE,"E43");var subQ7=makeQuery(id+"F21.imprint","INTERSECT",VERTEX,{"derivedFrom":[makeQuery(id+"F20.boolean.opBoolean","COPY",EDGE,{"derivedFrom":makeQuery(id+"F20.opExtrude","CAP_EDGE",EDGE,{"disambiguationData":[OSD([sQuery(id+"F19.wireOp",EDGE,"E38")])],"isStart":true})}),subQ1]});Q0=makeQuery(id+"F21.imprint","IMPRINT",FACE,{"disambiguationData":[TD([[makeQuery(id+"F21.imprint","IMPRINT",EDGE,{"disambiguationData":[TD([[subQ7,1.0]])],"derivedFrom":subQ1}),-1.0]])]});}
            var Q1;
            {var subQ0=sQuery(id+"F21.wireOp",EDGE,"E45.1");var subQ1=sQuery(id+"F21.wireOp",EDGE,"E43");var subQ2=makeQuery(id+"F21.imprint","INTERSECT",VERTEX,{"derivedFrom":[subQ1,subQ0]});Q1=makeQuery(id+"F21.imprint","IMPRINT",FACE,{"disambiguationData":[TD([[makeQuery(id+"F21.imprint","IMPRINT",EDGE,{"disambiguationData":[TD([[subQ2,-1.0]])],"derivedFrom":subQ1}),-1.0]])]});}
            var Q2;
            {var subQ0=sQuery(id+"F21.wireOp",EDGE,"E43");var subQ1=makeQuery(id+"F18.boolean.opBoolean","COPY",EDGE,{"derivedFrom":makeQuery(id+"F18.opExtrude","CAP_EDGE",EDGE,{"disambiguationData":[OSD([sQuery(id+"F17.wireOp",EDGE,"E36.top")])],"isStart":true})});var subQ2=makeQuery(id+"F21.imprint","INTERSECT",VERTEX,{"derivedFrom":[subQ1,subQ0]});Q2=makeQuery(id+"F21.imprint","IMPRINT",FACE,{"disambiguationData":[TD([[makeQuery(id+"F21.imprint","IMPRINT",EDGE,{"disambiguationData":[TD([[subQ2,1.0]])],"derivedFrom":subQ0}),-1.0]])]});}
            var Q3;
            {var subQ0=sQuery(id+"F21.wireOp",EDGE,"E43");var subQ8=makeQuery(id+"F21.imprint","INTERSECT",VERTEX,{"derivedFrom":[makeQuery(id+"F20.boolean.opBoolean","COPY",EDGE,{"derivedFrom":makeQuery(id+"F20.opExtrude","CAP_EDGE",EDGE,{"disambiguationData":[OSD([sQuery(id+"F19.wireOp",EDGE,"E39.1.0")])],"isStart":true})}),subQ0]});Q3=makeQuery(id+"F21.imprint","IMPRINT",FACE,{"disambiguationData":[TD([[makeQuery(id+"F21.imprint","IMPRINT",EDGE,{"disambiguationData":[TD([[subQ8,1.0]])],"derivedFrom":subQ0}),-1.0]])]});}
            var Q4;
            {var subQ7=sQuery(id+"F21.wireOp",EDGE,"E45.0");Q4=makeQuery(id+"F21.imprint","IMPRINT",FACE,{"disambiguationData":[TD([[makeQuery(id+"F21.imprint","IMPRINT",EDGE,{"derivedFrom":subQ7}),1.0]])]});}
            var Q5;
            {var subQ1=sQuery(id+"F21.wireOp",EDGE,"E45.0");Q5=makeQuery(id+"F21.imprint","IMPRINT",FACE,{"disambiguationData":[TD([[makeQuery(id+"F21.imprint","IMPRINT",EDGE,{"derivedFrom":subQ1}),-1.0]])]});}
            var Q6;
            {var subQ0=sQuery(id+"F21.wireOp",EDGE,"E45.1");var subQ1=sQuery(id+"F21.wireOp",EDGE,"E43");var subQ2=makeQuery(id+"F21.imprint","INTERSECT",VERTEX,{"derivedFrom":[subQ1,subQ0]});Q6=makeQuery(id+"F21.imprint","IMPRINT",FACE,{"disambiguationData":[TD([[makeQuery(id+"F21.imprint","IMPRINT",EDGE,{"disambiguationData":[TD([[subQ2,-1.0]])],"derivedFrom":subQ1}),1.0]])]});}
            var Q7;
            {var subQ0=sQuery(id+"F21.wireOp",EDGE,"E45.3");var subQ1=sQuery(id+"F21.wireOp",EDGE,"E43");var subQ2=makeQuery(id+"F21.imprint","INTERSECT",VERTEX,{"derivedFrom":[subQ1,subQ0]});Q7=makeQuery(id+"F21.imprint","IMPRINT",FACE,{"disambiguationData":[TD([[makeQuery(id+"F21.imprint","IMPRINT",EDGE,{"disambiguationData":[TD([[subQ2,1.0]])],"derivedFrom":subQ1}),1.0]])]});}
            var Q8;
            {var subQ0=sQuery(id+"F21.wireOp",EDGE,"E43");var subQ1=sQuery(id+"F19.wireOp",EDGE,"E39.9.0");var subQ2=makeQuery(id+"F20.boolean.opBoolean","COPY",EDGE,{"derivedFrom":makeQuery(id+"F20.opExtrude","CAP_EDGE",EDGE,{"disambiguationData":[OSD([subQ1])],"isStart":true})});var subQ3=makeQuery(id+"F21.imprint","INTERSECT",VERTEX,{"derivedFrom":[subQ2,subQ0]});Q8=makeQuery(id+"F21.imprint","IMPRINT",FACE,{"disambiguationData":[TD([[makeQuery(id+"F21.imprint","IMPRINT",EDGE,{"disambiguationData":[TD([[subQ3,-1.0]])],"derivedFrom":subQ0}),1.0]])]});}
            var Q9;
            {var subQ0=sQuery(id+"F21.wireOp",EDGE,"E43");var subQ1=sQuery(id+"F19.wireOp",EDGE,"E38");var subQ2=makeQuery(id+"F20.boolean.opBoolean","COPY",EDGE,{"derivedFrom":makeQuery(id+"F20.opExtrude","CAP_EDGE",EDGE,{"disambiguationData":[OSD([subQ1])],"isStart":true})});var subQ3=makeQuery(id+"F21.imprint","INTERSECT",VERTEX,{"derivedFrom":[subQ2,subQ0]});Q9=makeQuery(id+"F21.imprint","IMPRINT",FACE,{"disambiguationData":[TD([[makeQuery(id+"F21.imprint","IMPRINT",EDGE,{"disambiguationData":[TD([[subQ3,1.0]])],"derivedFrom":subQ0}),1.0]])]});}
            extrude(context, id + "F22", {"entities" : qUnion([Q0, Q1, Q2, Q3, Q4, Q5, Q6, Q7, Q8, Q9]), "operationType" : NewBodyOperationType.REMOVE, "oppositeDirection" : true, "depth" : 6 * mm});
        }
    });
